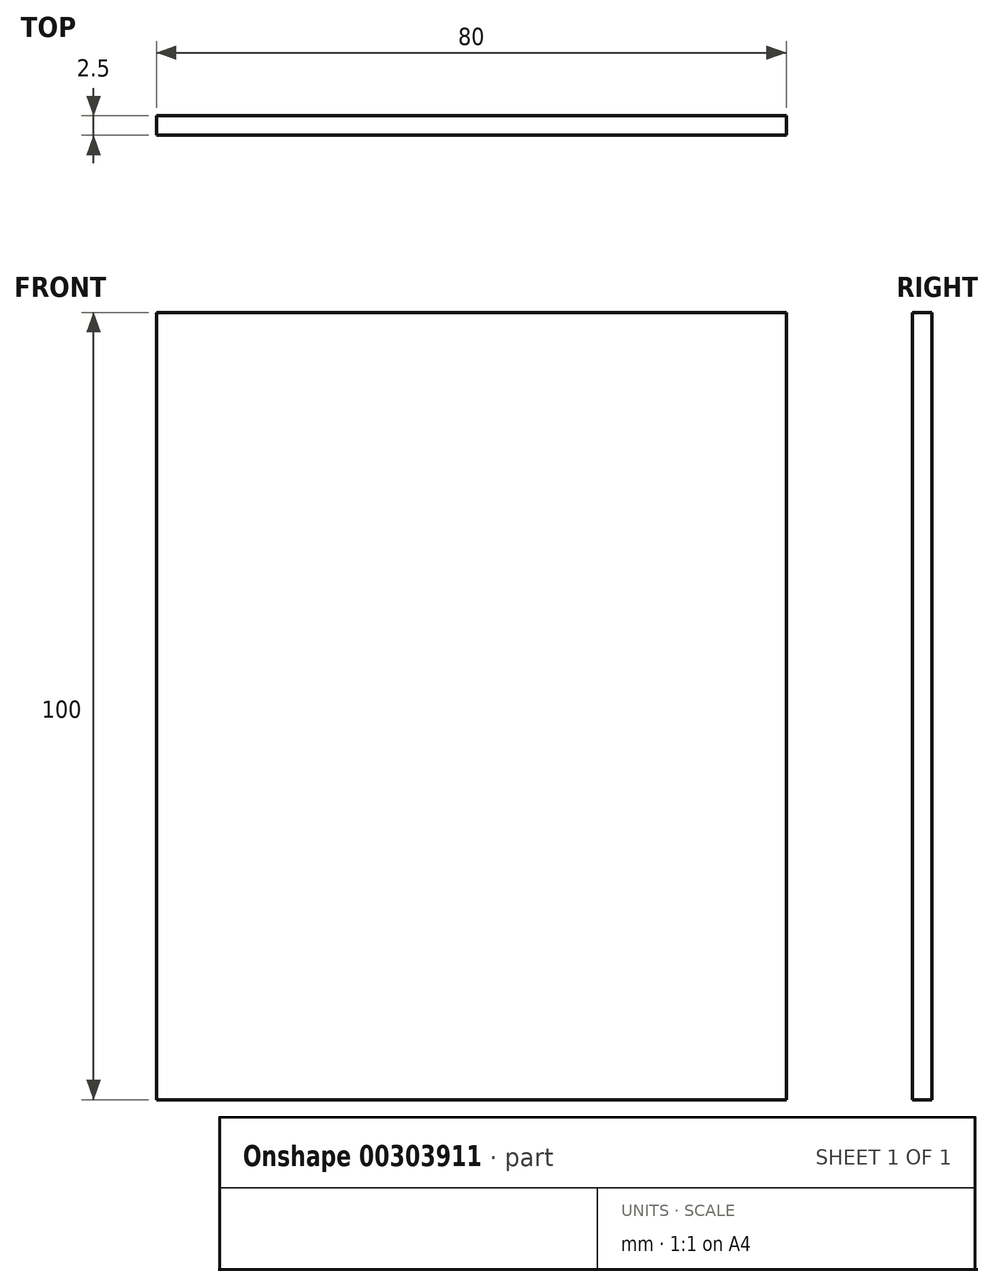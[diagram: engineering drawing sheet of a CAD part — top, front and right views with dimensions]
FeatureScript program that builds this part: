
annotation { "Feature Type Name" : "Feature", "Feature Type Description" : "" }
export const myFeature = defineFeature(function(context is Context, id is Id, definition is map)
    precondition{}
    {
        {
            var Q0;
            Q0=qCreatedBy(makeId("Front.planeOp"),FACE);
            var sketch = newSketch(context, id + "F0", { "sketchPlane" : qUnion([Q0])});
            skLineSegment(sketch, "E0.bottom", {"start": v(-80, 71.73) * mm, "end": v(0, 71.73) * mm});
            skLineSegment(sketch, "E0.top", {"start": v(-80, -28.27) * mm, "end": v(0, -28.27) * mm});
            skLineSegment(sketch, "E0.left", {"start": v(-80, 71.73) * mm, "end": v(-80, -28.27) * mm});
            skLineSegment(sketch, "E0.right", {"start": v(0, 71.73) * mm, "end": v(0, -28.27) * mm});
            skSolve(sketch);
        }
        {
            var Q0;
            Q0=makeQuery(id+"F0.imprint","IMPRINT",FACE,{"disambiguationData":[TD([[makeQuery(id+"F0.imprint","IMPRINT",EDGE,{"derivedFrom":sQuery(id+"F0.wireOp",EDGE,"E0.bottom")}),-1.0]])]});
            extrude(context, id + "F1", {"entities" : qUnion([Q0]), "depth" : 2.5 * mm});
        }
    });
